# Revit family: STS-479_RV17_LOD400
name_source: partatom
category: Электрооборудование
revit_build: Autodesk Revit 2017 (Build: 20170118_1100(x64)
units: mm (PartAtom-declared; Revit-internal decimal feet)

## family parameters
Всегда вертикально = Да
Конфигурация панели = Два столбца, слева направо
На основе рабочей плоскости = Нет
Общий = Нет
При загрузке вырезать с полостями = Нет
Размер круглого соединителя = Использовать диаметр
Тип детали = Щит
Точка расчета площади = Нет

## types (1)
- STS-479
    ADSK_URL страницы изделия = https://stilsoft.ru
    ADSK_Единица измерения = шт.
    ADSK_Завод-изготовитель = ООО «Основа Безопасности»
    ADSK_Количество = 1
    ADSK_Марка = CТВФ.426484.072
    ADSK_Масса = 1
    ADSK_Наименование = Пульт управления STS-479
    ADSK_Размер_Высота = 138 мм
    ADSK_Размер_Глубина = 53 мм
    ADSK_Размер_Длина = 215 мм
    Диагональ экрана = 7”
    Диапазон рабочих температур, ˚С = от + 1 до + 40
От + 1 до + 40
    Количество абонентов, до, шт. = 50
    Максимальный потребляемый ток, не более, А = 1.5
    Напряжение = 12
    Разрешение экрана, пикс = 1024х600
